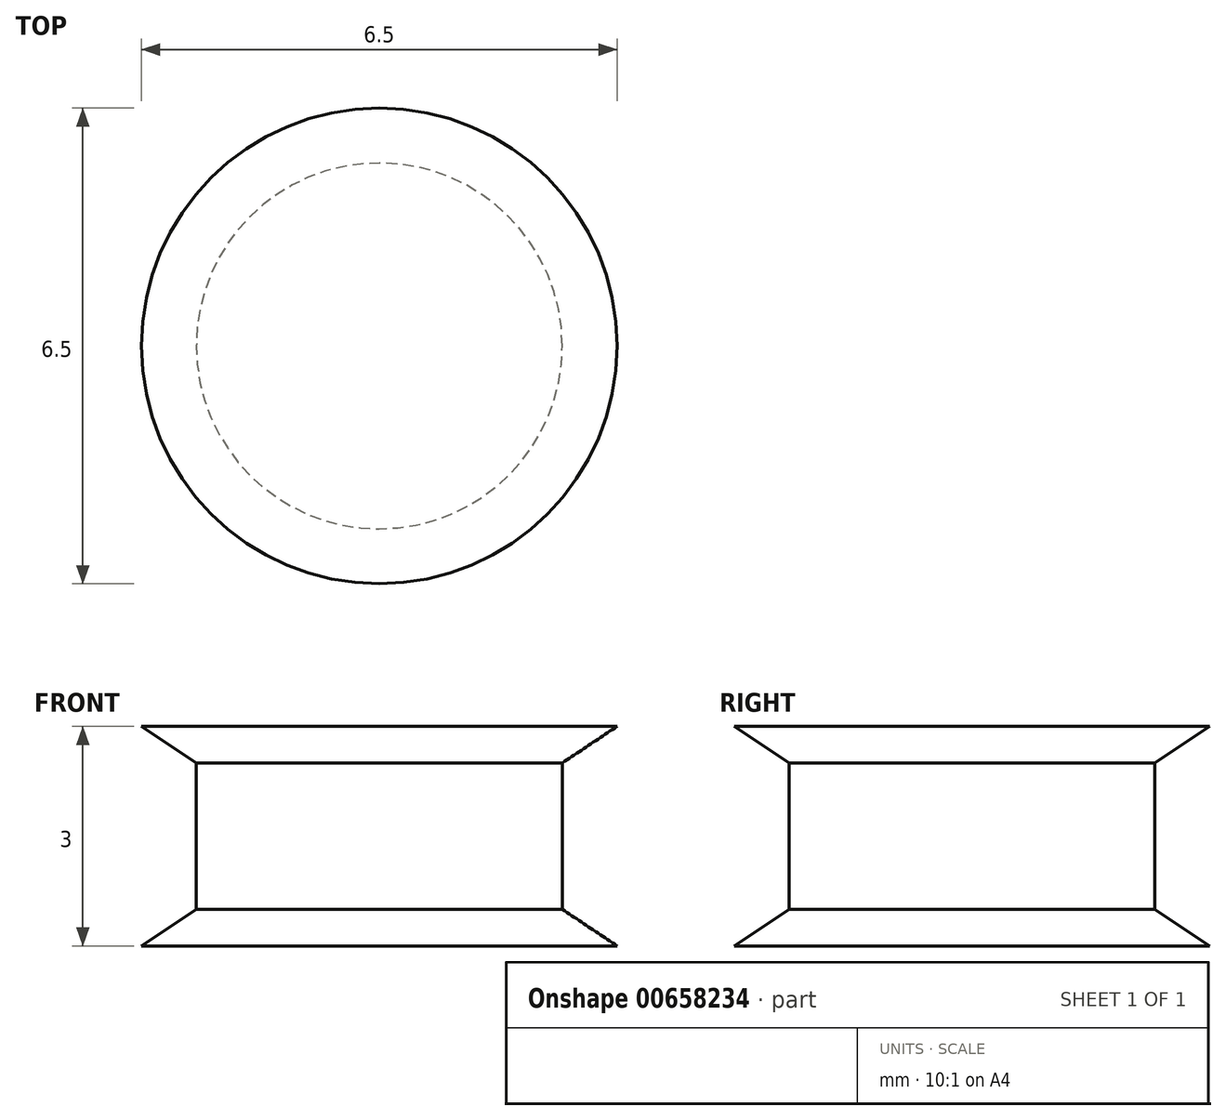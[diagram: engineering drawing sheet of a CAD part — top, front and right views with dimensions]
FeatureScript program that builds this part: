
annotation { "Feature Type Name" : "Feature", "Feature Type Description" : "" }
export const myFeature = defineFeature(function(context is Context, id is Id, definition is map)
    precondition{}
    {
        {
            var Q0;
            Q0=qCreatedBy(makeId("Top.planeOp"),FACE);
            var sketch = newSketch(context, id + "F0", { "sketchPlane" : qUnion([Q0])});
            skCircle(sketch, "E0", {"center": v(0, 0) * mm, "radius": 2.5 * mm});
            skCircle(sketch, "E1", {"center": v(0, 0) * mm, "radius": 3.25 * mm});
            skSolve(sketch);
        }
        {
            var Q0;
            Q0=makeQuery(id+"F0.imprint","IMPRINT",FACE,{"disambiguationData":[TD([[makeQuery(id+"F0.imprint","IMPRINT",EDGE,{"derivedFrom":sQuery(id+"F0.wireOp",EDGE,"E0")}),1.0]])]});
            extrude(context, id + "F1", {"entities" : qUnion([Q0]), "oppositeDirection" : true, "depth" : 3 * mm, "offsetDistance" : 25 * mm});
        }
        {
            var Q0;
            Q0=makeQuery(id+"F0.imprint","IMPRINT",FACE,{"disambiguationData":[TD([[makeQuery(id+"F0.imprint","IMPRINT",EDGE,{"derivedFrom":sQuery(id+"F0.wireOp",EDGE,"E0")}),-1.0]])]});
            extrude(context, id + "F2", {"entities" : qUnion([Q0]), "operationType" : NewBodyOperationType.ADD, "oppositeDirection" : true, "depth" : 3 * mm, "offsetDistance" : 25 * mm, "hasSecondDirection" : true, "secondDirectionOppositeDirection" : true, "secondDirectionDepth" : 2.5 * mm});
        }
        {
            var Q0;
            Q0=makeQuery(id+"F0.imprint","IMPRINT",FACE,{"disambiguationData":[TD([[makeQuery(id+"F0.imprint","IMPRINT",EDGE,{"derivedFrom":sQuery(id+"F0.wireOp",EDGE,"E0")}),-1.0]])]});
            extrude(context, id + "F3", {"entities" : qUnion([Q0]), "operationType" : NewBodyOperationType.ADD, "oppositeDirection" : true, "depth" : 0.5 * mm, "offsetDistance" : 25 * mm});
        }
        {
            var Q0;
            Q0=makeQuery(id+"F3.opExtrude","CAP_EDGE",EDGE,{"disambiguationData":[OSD([sQuery(id+"F0.wireOp",EDGE,"E1")])],"isStart":false});
            chamfer(context, id + "F4", {"entities" : qUnion([Q0]), "chamferType" : ChamferType.TWO_OFFSETS, "width1" : 0.5 * mm, "oppositeDirection" : false, "width2" : 0.75 * mm, "tangentPropagation" : true});
        }
        {
            var Q0;
            Q0=makeQuery(id+"F2.opExtrude","CAP_EDGE",EDGE,{"disambiguationData":[OSD([sQuery(id+"F0.wireOp",EDGE,"E1")])],"isStart":true});
            chamfer(context, id + "F5", {"entities" : qUnion([Q0]), "chamferType" : ChamferType.TWO_OFFSETS, "width1" : 0.75 * mm, "oppositeDirection" : false, "width2" : 0.5 * mm, "tangentPropagation" : true});
        }
    });
